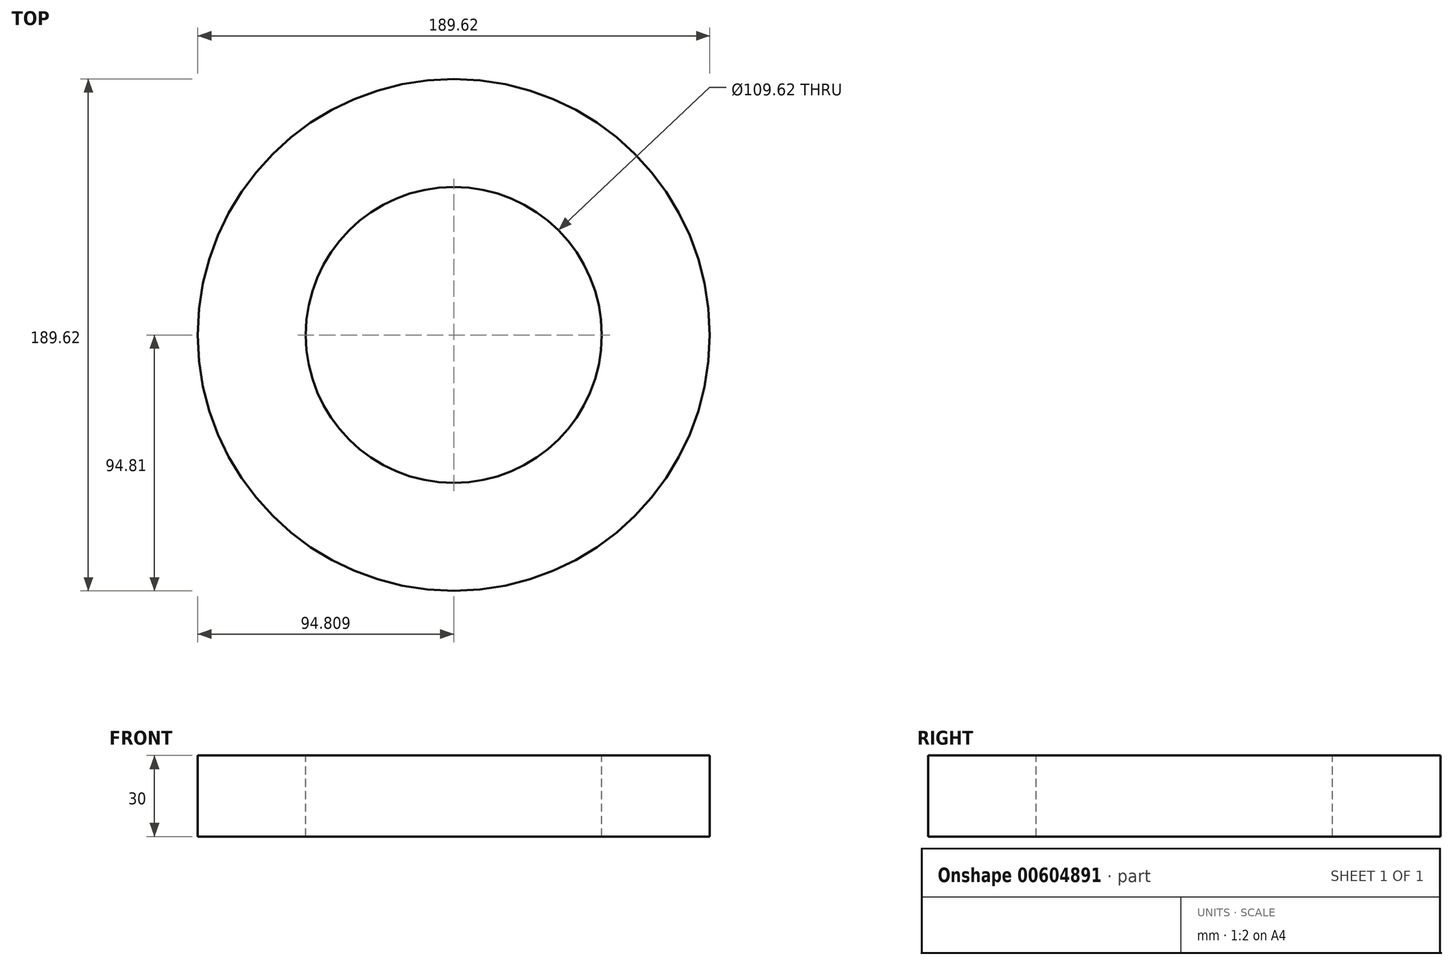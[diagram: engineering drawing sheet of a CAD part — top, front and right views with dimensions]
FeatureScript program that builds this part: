
annotation { "Feature Type Name" : "Feature", "Feature Type Description" : "" }
export const myFeature = defineFeature(function(context is Context, id is Id, definition is map)
    precondition{}
    {
        {
            var Q0;
            Q0=qCreatedBy(makeId("Front.planeOp"),FACE);
            var sketch = newSketch(context, id + "F0", { "sketchPlane" : qUnion([Q0])});
            skLineSegment(sketch, "E0.bottom", {"start": v(20, -15) * mm, "end": v(-20, -15) * mm});
            skLineSegment(sketch, "E0.top", {"start": v(20, 15) * mm, "end": v(-20, 15) * mm});
            skLineSegment(sketch, "E0.left", {"start": v(20, -15) * mm, "end": v(20, 15) * mm});
            skLineSegment(sketch, "E0.right", {"start": v(-20, -15) * mm, "end": v(-20, 15) * mm});
            skPoint(sketch, "E0.middle", {"position": v(0, 0) * mm});
            skSolve(sketch);
        }
        {
            var Q0;
            Q0=qCreatedBy(makeId("Front.planeOp"),FACE);
            var sketch = newSketch(context, id + "F1", { "sketchPlane" : qUnion([Q0])});
            skLineSegment(sketch, "E1", {"start": v(74.8, 27.31) * mm, "end": v(74.8, -33.3) * mm});
            skSolve(sketch);
        }
        {
            var Q0;
            Q0=makeQuery(id+"F0.imprint","IMPRINT",FACE,{"disambiguationData":[TD([[makeQuery(id+"F0.imprint","IMPRINT",EDGE,{"derivedFrom":sQuery(id+"F0.wireOp",EDGE,"E0.bottom")}),-1.0]])]});
            var Q1;
            Q1=sQuery(id+"F1.wireOp",EDGE,"E1");
            revolve(context, id + "F2", {"entities" : qUnion([Q0]), "axis" : qUnion([Q1]), "revolveType" : RevolveType.FULL});
        }
    });
